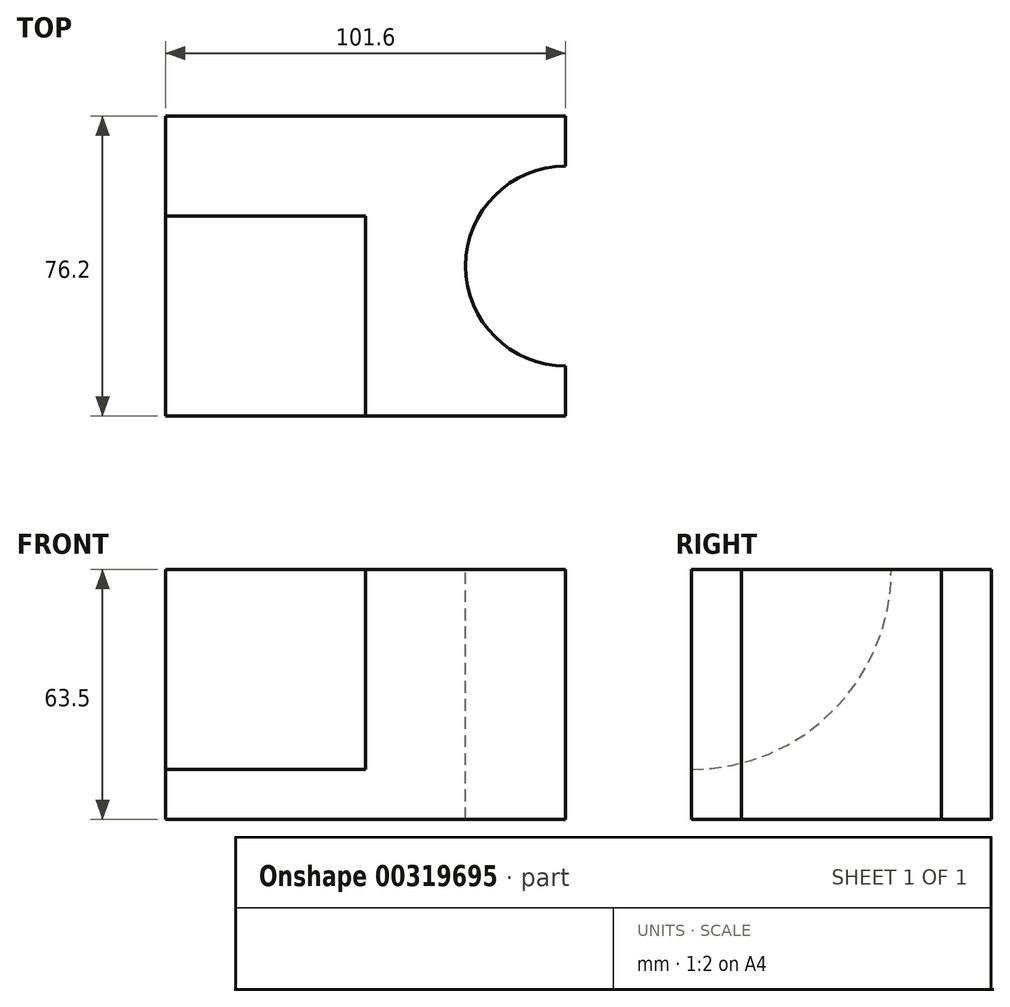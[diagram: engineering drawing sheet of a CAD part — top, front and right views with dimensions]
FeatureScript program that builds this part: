
annotation { "Feature Type Name" : "Feature", "Feature Type Description" : "" }
export const myFeature = defineFeature(function(context is Context, id is Id, definition is map)
    precondition{}
    {
        {
            var Q0;
            Q0=qCreatedBy(makeId("Top.planeOp"),FACE);
            var sketch = newSketch(context, id + "F0", { "sketchPlane" : qUnion([Q0])});
            skLineSegment(sketch, "E0", {"start": v(-44.42, 49.5) * mm, "end": v(57.18, 49.5) * mm});
            skLineSegment(sketch, "E1", {"start": v(57.18, 49.5) * mm, "end": v(57.18, -26.7) * mm});
            skLineSegment(sketch, "E2", {"start": v(-44.42, 49.5) * mm, "end": v(-44.42, -26.7) * mm});
            skLineSegment(sketch, "E3", {"start": v(-44.42, -26.7) * mm, "end": v(57.18, -26.7) * mm});
            skSolve(sketch);
        }
        {
            var Q0;
            Q0=makeQuery(id+"F0.imprint","IMPRINT",FACE,{"disambiguationData":[TD([[makeQuery(id+"F0.imprint","IMPRINT",EDGE,{"derivedFrom":sQuery(id+"F0.wireOp",EDGE,"E0")}),-1.0]])]});
            extrude(context, id + "F1", {"entities" : qUnion([Q0]), "depth" : 63.5 * mm});
        }
        {
            var Q0;
            Q0=makeQuery(id+"F1.opExtrude","CAP_FACE",FACE,{"disambiguationData":[OSD([sQuery(id+"F0.wireOp",EDGE,"E0"),sQuery(id+"F0.wireOp",EDGE,"E1"),sQuery(id+"F0.wireOp",EDGE,"E2"),sQuery(id+"F0.wireOp",EDGE,"E3")])],"isStart":false});
            var sketch = newSketch(context, id + "F2", { "sketchPlane" : qUnion([Q0])});
            skArc(sketch, "E4", {"start": v(57.18, 36.8) * mm, "mid": v(31.78, 11.4) * mm, "end": v(57.18, -14) * mm});
            skLineSegment(sketch, "E5", {"start": v(57.18, 36.8) * mm, "end": v(57.18, -14) * mm});
            skSolve(sketch);
        }
        {
            var Q0;
            Q0=makeQuery(id+"F2.imprint","IMPRINT",FACE,{"disambiguationData":[TD([[makeQuery(id+"F2.imprint","IMPRINT",EDGE,{"derivedFrom":sQuery(id+"F2.wireOp",EDGE,"E4")}),1.0]])]});
            extrude(context, id + "F3", {"entities" : qUnion([Q0]), "operationType" : NewBodyOperationType.REMOVE, "endBound" : BoundingType.THROUGH_ALL, "oppositeDirection" : true, "depth" : 25.4 * mm});
        }
        {
            var Q0;
            Q0=makeQuery(id+"F1.opExtrude","SWEPT_FACE",FACE,{"disambiguationData":[OSD([sQuery(id+"F0.wireOp",EDGE,"E2")])]});
            var sketch = newSketch(context, id + "F4", { "sketchPlane" : qUnion([Q0])});
            skArc(sketch, "E6", {"start": v(-24.1, 63.5) * mm, "mid": v(-9.23, 27.58) * mm, "end": v(26.7, 12.7) * mm});
            skLineSegment(sketch, "E7", {"start": v(-24.1, 63.5) * mm, "end": v(26.7, 63.5) * mm});
            skLineSegment(sketch, "E8", {"start": v(26.7, 63.5) * mm, "end": v(26.7, 12.7) * mm});
            skSolve(sketch);
        }
        {
            var Q0;
            Q0=makeQuery(id+"F4.imprint","IMPRINT",FACE,{"disambiguationData":[TD([[makeQuery(id+"F4.imprint","IMPRINT",EDGE,{"derivedFrom":sQuery(id+"F4.wireOp",EDGE,"E6")}),1.0]])]});
            extrude(context, id + "F5", {"entities" : qUnion([Q0]), "operationType" : NewBodyOperationType.REMOVE, "oppositeDirection" : true, "depth" : 50.8 * mm});
        }
    });
